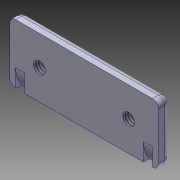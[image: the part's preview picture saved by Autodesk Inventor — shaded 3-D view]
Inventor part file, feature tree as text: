
AUTODESK INVENTOR PART (.ipt)
format: ipt  version: 2013 (Build 170138000, 138)  size: 122,880 bytes
history: native  units: mm
features: sketch x3, extrude x1, hole x1, plane x1, revolve x1, fillet x1, mirror x1
ambient origin geometry x8: Origin, YZ Plane, XZ Plane, XY Plane, X Axis, Y Axis, Z Axis, Center Point
bodies: Solid1 (feature_tree)
feature tree (9):
  extrude  "Extrusion1"  Depth=25.0mm
  hole  "Hole1"  [1 undecoded]
  plane  "Work Plane1"
  revolve  "Revolution1"  [1 undecoded]
  fillet  "Fillet1"  [1 undecoded]
  mirror  "Mirror1"
  sketch  "Sketch1"  dims[d0=10.0mm d2=25.0mm]
  sketch  "Sketch2"  dims[d3=2.0mm d4=0.0mm d5=5.0mm]
  sketch  "Sketch4"  dims[d6=2.013mm d7=6.0mm d8=4.0mm d9=2.0mm d10=90.0deg d11=8.0mm d12=20.594885mm d13=1.0mm d14=-5.0mm d15=3.0mm d16=5.0mm d17=5.0mm d18=1.5mm d19=1.0mm d20=90.0deg]
note: 3 required parameter values undecoded (feature->parameter linkage not recoverable at this tier; creation-order binding heuristic only, values carry confidence <= 0.55)